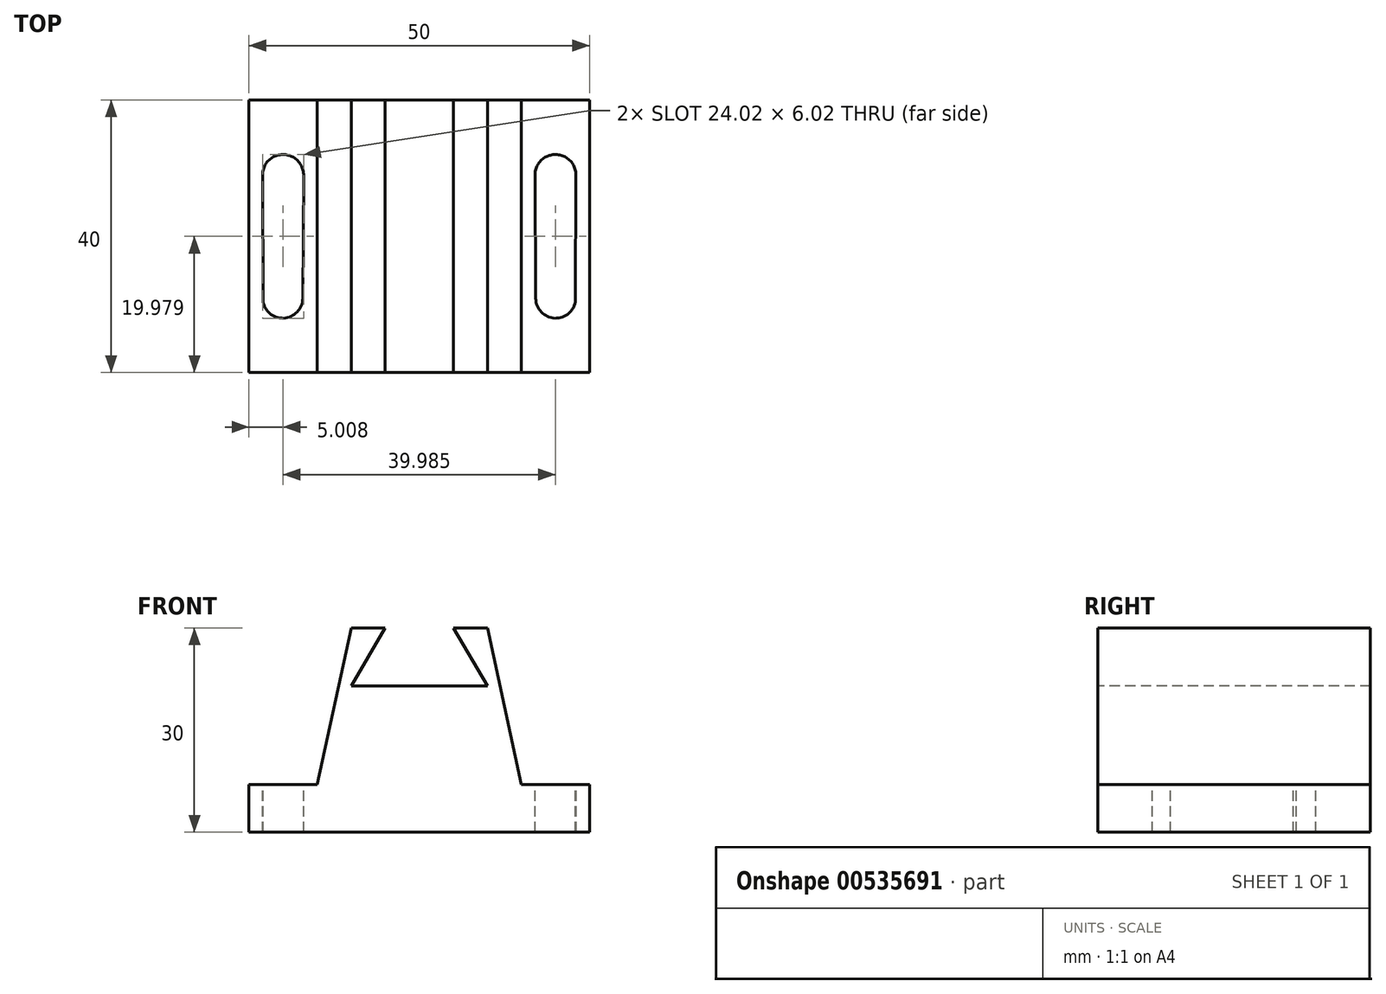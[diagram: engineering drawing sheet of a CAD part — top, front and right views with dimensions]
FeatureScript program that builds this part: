
annotation { "Feature Type Name" : "Feature", "Feature Type Description" : "" }
export const myFeature = defineFeature(function(context is Context, id is Id, definition is map)
    precondition{}
    {
        {
            var Q0;
            Q0=qCreatedBy(makeId("Front.planeOp"),FACE);
            var sketch = newSketch(context, id + "F0", { "sketchPlane" : qUnion([Q0])});
            skLineSegment(sketch, "E0.bottom", {"start": v(25, -15) * mm, "end": v(-25, -15) * mm});
            skLineSegment(sketch, "E0.top", {"start": v(25, 15) * mm, "end": v(-25, 15) * mm});
            skLineSegment(sketch, "E0.left", {"start": v(25, -15) * mm, "end": v(25, 15) * mm});
            skLineSegment(sketch, "E0.right", {"start": v(-25, -15) * mm, "end": v(-25, 15) * mm});
            skPoint(sketch, "E0.middle", {"position": v(0, 0) * mm});
            skSolve(sketch);
        }
        {
            var Q0;
            Q0 = qSketchRegion(id + "F0", true);
            extrude(context, id + "F1", {"entities" : qUnion([Q0]), "depth" : 40 * mm, "offsetDistance" : 25 * mm});
        }
        {
            var Q0;
            Q0=makeQuery(id+"F1.opExtrude","CAP_FACE",FACE,{"disambiguationData":[OSD([sQuery(id+"F0.wireOp",EDGE,"E0.bottom"),sQuery(id+"F0.wireOp",EDGE,"E0.top"),sQuery(id+"F0.wireOp",EDGE,"E0.left"),sQuery(id+"F0.wireOp",EDGE,"E0.right")])],"isStart":false});
            var sketch = newSketch(context, id + "F2", { "sketchPlane" : qUnion([Q0])});
            skLineSegment(sketch, "E1", {"start": v(-25, -8) * mm, "end": v(-15, -8) * mm});
            skLineSegment(sketch, "E2", {"start": v(15, -8) * mm, "end": v(25, -8) * mm});
            skLineSegment(sketch, "E3", {"start": v(-15, -8) * mm, "end": v(-15, 15) * mm});
            skLineSegment(sketch, "E4", {"start": v(15, -8) * mm, "end": v(15, 15) * mm});
            skSolve(sketch);
        }
        {
            var Q0;
            {var subQ0=sQuery(id+"F2.wireOp",EDGE,"E1");Q0=makeQuery(id+"F2.imprint","IMPRINT",FACE,{"disambiguationData":[TD([[makeQuery(id+"F2.imprint","IMPRINT",EDGE,{"derivedFrom":subQ0}),1.0]])]});}
            var Q1;
            {var subQ0=sQuery(id+"F2.wireOp",EDGE,"E2");Q1=makeQuery(id+"F2.imprint","IMPRINT",FACE,{"disambiguationData":[TD([[makeQuery(id+"F2.imprint","IMPRINT",EDGE,{"derivedFrom":subQ0}),1.0]])]});}
            extrude(context, id + "F3", {"entities" : qUnion([Q0, Q1]), "operationType" : NewBodyOperationType.REMOVE, "endBound" : BoundingType.THROUGH_ALL, "oppositeDirection" : true, "depth" : 25 * mm, "offsetDistance" : 25 * mm});
        }
        {
            var Q0;
            Q0=makeQuery(id+"F3.boolean.opBoolean","COPY",FACE,{"derivedFrom":makeQuery(id+"F3.opExtrude","SWEPT_FACE",FACE,{"disambiguationData":[OSD([sQuery(id+"F2.wireOp",EDGE,"E1")])]})});
            var sketch = newSketch(context, id + "F4", { "sketchPlane" : qUnion([Q0])});
            skLineSegment(sketch, "E5", {"start": v(-33.08, -8) * mm, "end": v(-13.15, -8) * mm, "construction": true});
            skLineSegment(sketch, "E6", {"start": v(-32.35, -32) * mm, "end": v(-13.22, -32) * mm, "construction": true});
            skLineSegment(sketch, "E7", {"start": v(-25, -40) * mm, "end": v(-22.12, -40) * mm, "construction": true});
            skPoint(sketch, "E8.endSnap0", {"position": v(-22.12, 0) * mm});
            skPoint(sketch, "E9.endSnap0", {"position": v(-23.12, -8) * mm});
            skLineSegment(sketch, "E10", {"start": v(-25, 0) * mm, "end": v(-22.12, 0) * mm, "construction": true});
            skLineSegment(sketch, "E11", {"start": v(-15, 0) * mm, "end": v(-16.12, 0) * mm, "construction": true});
            skLineSegment(sketch, "E12", {"start": v(-20, 5.37) * mm, "end": v(-20, -48.46) * mm, "construction": true});
            skArc(sketch, "E13", {"start": v(-16.98, -10.89) * mm, "mid": v(-20.23, -8) * mm, "end": v(-23, -11.35) * mm});
            skPoint(sketch, "E14.startSnap0", {"position": v(-25, -20) * mm});
            skPoint(sketch, "E14.endSnap0", {"position": v(-15, -20) * mm});
            skArc(sketch, "E15.MirrorC", {"start": v(-17.1, -29.13) * mm, "mid": v(-19.92, -32.03) * mm, "end": v(-22.95, -29.37) * mm});
            skLineSegment(sketch, "E16", {"start": v(-23, -11.35) * mm, "end": v(-22.95, -29.37) * mm});
            skLineSegment(sketch, "E17", {"start": v(-16.98, -10.89) * mm, "end": v(-17.1, -29.13) * mm});
            skLineSegment(sketch, "E18", {"start": v(0, 2.73) * mm, "end": v(0, -51.69) * mm, "construction": true});
            skLineSegment(sketch, "E19.MirrorCS", {"start": v(16.98, -10.89) * mm, "end": v(17.1, -29.13) * mm});
            skLineSegment(sketch, "E20.MirrorCS", {"start": v(23, -11.35) * mm, "end": v(22.95, -29.37) * mm});
            skArc(sketch, "E21.MirrorCS", {"start": v(16.98, -10.89) * mm, "mid": v(20.23, -8) * mm, "end": v(23, -11.35) * mm});
            skArc(sketch, "E22.MirrorCS", {"start": v(17.1, -29.13) * mm, "mid": v(19.92, -32.03) * mm, "end": v(22.95, -29.37) * mm});
            skSolve(sketch);
        }
        {
            var Q0;
            Q0=makeQuery(id+"F4.imprint","IMPRINT",FACE,{"disambiguationData":[TD([[makeQuery(id+"F4.imprint","IMPRINT",EDGE,{"derivedFrom":sQuery(id+"F4.wireOp",EDGE,"E13")}),1.0]])]});
            var Q1;
            Q1=makeQuery(id+"F4.imprint","IMPRINT",FACE,{"disambiguationData":[TD([[makeQuery(id+"F4.imprint","IMPRINT",EDGE,{"derivedFrom":sQuery(id+"F4.wireOp",EDGE,"E19.MirrorCS")}),1.0]])]});
            extrude(context, id + "F5", {"entities" : qUnion([Q0, Q1]), "operationType" : NewBodyOperationType.REMOVE, "endBound" : BoundingType.THROUGH_ALL, "oppositeDirection" : true, "depth" : 25 * mm, "offsetDistance" : 25 * mm});
        }
        {
            var Q0;
            Q0=makeQuery(id+"F1.opExtrude","CAP_FACE",FACE,{"disambiguationData":[OSD([sQuery(id+"F0.wireOp",EDGE,"E0.bottom"),sQuery(id+"F0.wireOp",EDGE,"E0.top"),sQuery(id+"F0.wireOp",EDGE,"E0.left"),sQuery(id+"F0.wireOp",EDGE,"E0.right")])],"isStart":false});
            var sketch = newSketch(context, id + "F6", { "sketchPlane" : qUnion([Q0])});
            skLineSegment(sketch, "E23", {"start": v(0, 21.33) * mm, "end": v(0, -27.77) * mm, "construction": true});
            skPoint(sketch, "E23.startSnap0", {"position": v(0, 15) * mm});
            skLineSegment(sketch, "E24", {"start": v(-10, 15) * mm, "end": v(-15, -8) * mm});
            skLineSegment(sketch, "E25.MirrorCS", {"start": v(10, 15) * mm, "end": v(15, -8) * mm});
            skSolve(sketch);
        }
        {
            var Q0;
            {var subQ0=sQuery(id+"F6.wireOp",EDGE,"E25.MirrorCS");var subQ1=makeQuery(id+"F3.boolean.opBoolean","COPY",EDGE,{"derivedFrom":makeQuery(id+"F3.opExtrude","CAP_EDGE",EDGE,{"disambiguationData":[OSD([sQuery(id+"F2.wireOp",EDGE,"E4")])],"isStart":true})});var subQ2=makeQuery(id+"F6.imprint","INTERSECT",VERTEX,{"derivedFrom":[subQ1,subQ0]});Q0=makeQuery(id+"F6.imprint","IMPRINT",FACE,{"disambiguationData":[TD([[makeQuery(id+"F6.imprint","IMPRINT",EDGE,{"disambiguationData":[TD([[subQ2,1.0]])],"derivedFrom":subQ0}),1.0]])]});}
            var Q1;
            {var subQ0=sQuery(id+"F6.wireOp",EDGE,"E24");Q1=makeQuery(id+"F6.imprint","IMPRINT",FACE,{"disambiguationData":[TD([[makeQuery(id+"F6.imprint","IMPRINT",EDGE,{"derivedFrom":subQ0}),-1.0]])]});}
            extrude(context, id + "F7", {"entities" : qUnion([Q0, Q1]), "operationType" : NewBodyOperationType.REMOVE, "endBound" : BoundingType.THROUGH_ALL, "oppositeDirection" : true, "depth" : 25 * mm, "offsetDistance" : 25 * mm});
        }
        {
            var Q0;
            {var subQ0=sQuery(id+"F6.wireOp",EDGE,"E24");Q0=makeQuery(id+"F6.imprint","IMPRINT",FACE,{"disambiguationData":[TD([[makeQuery(id+"F6.imprint","IMPRINT",EDGE,{"derivedFrom":subQ0}),-1.0]])]});}
            var Q1;
            {var subQ0=sQuery(id+"F6.wireOp",EDGE,"E25.MirrorCS");Q1=makeQuery(id+"F6.imprint","IMPRINT",FACE,{"disambiguationData":[TD([[makeQuery(id+"F6.imprint","IMPRINT",EDGE,{"derivedFrom":subQ0}),1.0]])]});}
            extrude(context, id + "F8", {"entities" : qUnion([Q0, Q1]), "operationType" : NewBodyOperationType.REMOVE, "endBound" : BoundingType.THROUGH_ALL, "depth" : 25 * mm, "offsetDistance" : 25 * mm});
        }
        {
            var Q0;
            Q0=makeQuery(id+"F1.opExtrude","CAP_FACE",FACE,{"disambiguationData":[OSD([sQuery(id+"F0.wireOp",EDGE,"E0.bottom"),sQuery(id+"F0.wireOp",EDGE,"E0.top"),sQuery(id+"F0.wireOp",EDGE,"E0.left"),sQuery(id+"F0.wireOp",EDGE,"E0.right")])],"isStart":false});
            var sketch = newSketch(context, id + "F9", { "sketchPlane" : qUnion([Q0])});
            skLineSegment(sketch, "E26", {"start": v(-10, 15) * mm, "end": v(-5, 15) * mm, "construction": true});
            skLineSegment(sketch, "E27", {"start": v(10, 15) * mm, "end": v(5, 15) * mm, "construction": true});
            skLineSegment(sketch, "E28", {"start": v(0, 26.55) * mm, "end": v(0, -28.05) * mm, "construction": true});
            skLineSegment(sketch, "E29", {"start": v(-10, 6.49) * mm, "end": v(0, 6.49) * mm});
            skLineSegment(sketch, "E30", {"start": v(-10, 6.49) * mm, "end": v(-5, 15) * mm});
            skLineSegment(sketch, "E31.MirrorCS", {"start": v(10, 6.49) * mm, "end": v(0, 6.49) * mm});
            skLineSegment(sketch, "E32.MirrorCS", {"start": v(10, 6.49) * mm, "end": v(5, 15) * mm});
            skSolve(sketch);
        }
        {
            var Q0;
            Q0=makeQuery(id+"F9.imprint","IMPRINT",FACE,{"disambiguationData":[TD([[makeQuery(id+"F9.imprint","IMPRINT",EDGE,{"derivedFrom":sQuery(id+"F9.wireOp",EDGE,"E29")}),1.0]])]});
            extrude(context, id + "F10", {"entities" : qUnion([Q0]), "operationType" : NewBodyOperationType.REMOVE, "endBound" : BoundingType.THROUGH_ALL, "oppositeDirection" : true, "depth" : 25 * mm, "offsetDistance" : 25 * mm});
        }
    });
